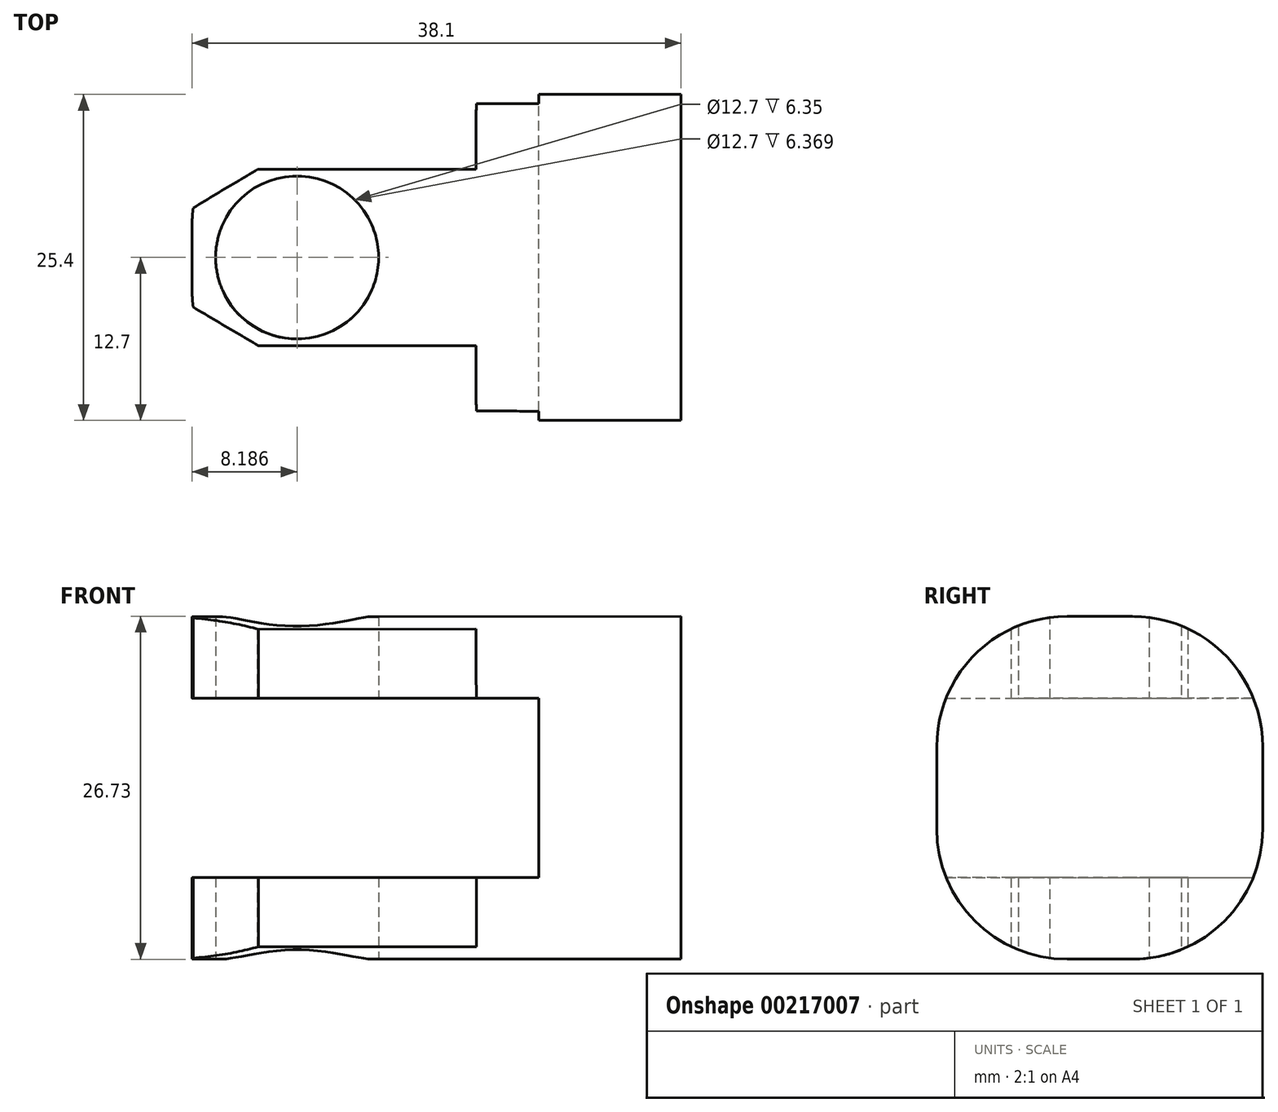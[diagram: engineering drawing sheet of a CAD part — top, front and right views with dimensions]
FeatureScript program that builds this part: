
annotation { "Feature Type Name" : "Feature", "Feature Type Description" : "" }
export const myFeature = defineFeature(function(context is Context, id is Id, definition is map)
    precondition{}
    {
        {
            var Q0;
            Q0=qCreatedBy(makeId("Front.planeOp"),FACE);
            var sketch = newSketch(context, id + "F0", { "sketchPlane" : qUnion([Q0])});
            skLineSegment(sketch, "E0.bottom", {"start": v(19.05, -6.98) * mm, "end": v(0, -6.99) * mm});
            skLineSegment(sketch, "E0.top", {"start": v(19.05, 6.99) * mm, "end": v(0, 6.99) * mm});
            skPoint(sketch, "E0.middle", {"position": v(0, 0) * mm});
            skLineSegment(sketch, "E1", {"start": v(0, 6.99) * mm, "end": v(0, 13.34) * mm});
            skLineSegment(sketch, "E2", {"start": v(0, -6.99) * mm, "end": v(0, -13.33) * mm});
            skLineSegment(sketch, "E3", {"start": v(0, -13.33) * mm, "end": v(38.1, -13.33) * mm});
            skLineSegment(sketch, "E4", {"start": v(38.1, -13.33) * mm, "end": v(38.1, 13.39) * mm});
            skLineSegment(sketch, "E5", {"start": v(38.1, 13.39) * mm, "end": v(0, 13.34) * mm});
            skPoint(sketch, "E0.right.end.orphan", {"position": v(-19.05, 6.99) * mm});
            skPoint(sketch, "E6.orphan", {"position": v(-19.05, -6.99) * mm});
            skLineSegment(sketch, "E7", {"start": v(19.05, 6.99) * mm, "end": v(27, 6.99) * mm});
            skLineSegment(sketch, "E8", {"start": v(27, 6.99) * mm, "end": v(27, -8.58) * mm});
            skLineSegment(sketch, "E9", {"start": v(19.05, -6.98) * mm, "end": v(27, -6.98) * mm});
            skSolve(sketch);
        }
        {
            var Q0;
            Q0 = qSketchRegion(id + "F0", true);
            extrude(context, id + "F1", {"entities" : qUnion([Q0]), "depth" : 25.4 * mm});
        }
        {
            var Q0;
            Q0=makeQuery(id+"F1.opExtrude","SWEPT_FACE",FACE,{"disambiguationData":[OSD([sQuery(id+"F0.wireOp",EDGE,"E3")])]});
            var sketch = newSketch(context, id + "F2", { "sketchPlane" : qUnion([Q0])});
            skCircle(sketch, "E10", {"center": v(8.19, 12.7) * mm, "radius": 6.35 * mm});
            skPoint(sketch, "E10.centerSnap0", {"position": v(0, 12.7) * mm});
            skSolve(sketch);
        }
        {
            var Q0;
            Q0=makeQuery(id+"F1.opExtrude","CAP_EDGE",EDGE,{"disambiguationData":[OSD([sQuery(id+"F0.wireOp",EDGE,"E2")])],"isStart":true});
            var Q1;
            Q1=makeQuery(id+"F1.opExtrude","CAP_EDGE",EDGE,{"disambiguationData":[OSD([sQuery(id+"F0.wireOp",EDGE,"E1")])],"isStart":true});
            var Q2;
            Q2=makeQuery(id+"F1.opExtrude","CAP_EDGE",EDGE,{"disambiguationData":[OSD([sQuery(id+"F0.wireOp",EDGE,"E1")])],"isStart":false});
            var Q3;
            Q3=makeQuery(id+"F1.opExtrude","CAP_EDGE",EDGE,{"disambiguationData":[OSD([sQuery(id+"F0.wireOp",EDGE,"E2")])],"isStart":false});
            fillet(context, id + "F3", {"entities" : qUnion([Q0, Q1, Q2, Q3]), "radius" : 10.16 * mm, "tangentPropagation" : true, "allowEdgeOverflow" : false});
        }
        {
            var Q0;
            Q0=makeQuery(id+"F2.imprint","IMPRINT",FACE,{"disambiguationData":[TD([[makeQuery(id+"F2.imprint","IMPRINT",EDGE,{"derivedFrom":sQuery(id+"F2.wireOp",EDGE,"E10")}),1.0]])]});
            extrude(context, id + "F4", {"entities" : qUnion([Q0]), "operationType" : NewBodyOperationType.REMOVE, "endBound" : BoundingType.THROUGH_ALL, "oppositeDirection" : true, "depth" : 25.4 * mm});
        }
        {
            var Q0;
            Q0=makeQuery(id+"F1.opExtrude","SWEPT_FACE",FACE,{"disambiguationData":[OSD([sQuery(id+"F0.wireOp",EDGE,"E5")])]});
            var sketch = newSketch(context, id + "F5", { "sketchPlane" : qUnion([Q0])});
            skLineSegment(sketch, "E11.bottom", {"start": v(22.15, -5.82) * mm, "end": v(-18.45, -5.82) * mm});
            skLineSegment(sketch, "E11.top", {"start": v(22.15, -19.58) * mm, "end": v(-18.45, -19.58) * mm});
            skLineSegment(sketch, "E11.left", {"start": v(22.15, -5.82) * mm, "end": v(22.15, -19.58) * mm});
            skLineSegment(sketch, "E11.right", {"start": v(-18.45, -5.82) * mm, "end": v(-18.45, -19.58) * mm});
            skPoint(sketch, "E11.middle", {"position": v(1.85, -12.7) * mm});
            skLineSegment(sketch, "E12", {"start": v(22.15, -19.58) * mm, "end": v(22.15, -25.4) * mm});
            skLineSegment(sketch, "E13", {"start": v(22.15, -5.82) * mm, "end": v(22.15, 0) * mm});
            skLineSegment(sketch, "E14", {"start": v(-6.3, -19.58) * mm, "end": v(17.98, -30.66) * mm});
            skLineSegment(sketch, "E15", {"start": v(17.98, -30.66) * mm, "end": v(22.15, -25.4) * mm});
            skLineSegment(sketch, "E16", {"start": v(-7.33, -5.82) * mm, "end": v(20.42, 6.01) * mm});
            skLineSegment(sketch, "E17", {"start": v(20.42, 6.01) * mm, "end": v(22.15, 0) * mm});
            skSolve(sketch);
        }
        {
            var Q0;
            {var subQ7=sQuery(id+"F5.wireOp",EDGE,"E16");Q0=makeQuery(id+"F5.imprint","IMPRINT",FACE,{"disambiguationData":[TD([[makeQuery(id+"F5.imprint","IMPRINT",EDGE,{"derivedFrom":subQ7}),-1.0]])]});}
            var Q1;
            {var subQ0=sQuery(id+"F5.wireOp",EDGE,"E13");Q1=makeQuery(id+"F5.imprint","IMPRINT",FACE,{"disambiguationData":[TD([[makeQuery(id+"F5.imprint","IMPRINT",EDGE,{"derivedFrom":subQ0}),1.0]])]});}
            var Q2;
            {var subQ0=sQuery(id+"F5.wireOp",EDGE,"E12");Q2=makeQuery(id+"F5.imprint","IMPRINT",FACE,{"disambiguationData":[TD([[makeQuery(id+"F5.imprint","IMPRINT",EDGE,{"derivedFrom":subQ0}),-1.0]])]});}
            var Q3;
            {var subQ6=sQuery(id+"F5.wireOp",EDGE,"E14");Q3=makeQuery(id+"F5.imprint","IMPRINT",FACE,{"disambiguationData":[TD([[makeQuery(id+"F5.imprint","IMPRINT",EDGE,{"derivedFrom":subQ6}),1.0]])]});}
            extrude(context, id + "F6", {"entities" : qUnion([Q0, Q1, Q2, Q3]), "operationType" : NewBodyOperationType.REMOVE, "endBound" : BoundingType.THROUGH_ALL, "oppositeDirection" : true, "depth" : 25.4 * mm});
        }
        {
            var Q0;
            Q0=makeQuery(id+"F1.opExtrude","CAP_EDGE",EDGE,{"disambiguationData":[OSD([sQuery(id+"F0.wireOp",EDGE,"E5")])],"isStart":false});
            var Q1;
            Q1=makeQuery(id+"F1.opExtrude","CAP_EDGE",EDGE,{"disambiguationData":[OSD([sQuery(id+"F0.wireOp",EDGE,"E5")])],"isStart":true});
            var Q2;
            Q2=makeQuery(id+"F1.opExtrude","CAP_EDGE",EDGE,{"disambiguationData":[OSD([sQuery(id+"F0.wireOp",EDGE,"E3")])],"isStart":true});
            var Q3;
            Q3=makeQuery(id+"F1.opExtrude","CAP_EDGE",EDGE,{"disambiguationData":[OSD([sQuery(id+"F0.wireOp",EDGE,"E3")])],"isStart":false});
            fillet(context, id + "F7", {"entities" : qUnion([Q0, Q1, Q2, Q3]), "radius" : 10.16 * mm, "tangentPropagation" : true, "allowEdgeOverflow" : false});
        }
        {
            var Q0;
            Q0=qCreatedBy(makeId("Top.planeOp"),FACE);
            var sketch = newSketch(context, id + "F8", { "sketchPlane" : qUnion([Q0])});
            skLineSegment(sketch, "E18", {"start": v(6.35, -5.07) * mm, "end": v(-2.7, -10.52) * mm});
            skLineSegment(sketch, "E19", {"start": v(-2.7, -10.52) * mm, "end": v(-2.7, -14.92) * mm});
            skLineSegment(sketch, "E20", {"start": v(-2.7, -14.92) * mm, "end": v(6.35, -20.28) * mm});
            skLineSegment(sketch, "E21", {"start": v(6.35, -20.28) * mm, "end": v(-5.74, -20.28) * mm});
            skLineSegment(sketch, "E22", {"start": v(-5.74, -20.28) * mm, "end": v(-5.74, -5.07) * mm});
            skLineSegment(sketch, "E23", {"start": v(-5.74, -5.07) * mm, "end": v(6.35, -5.07) * mm});
            skSolve(sketch);
        }
        {
            var Q0;
            Q0=makeQuery(id+"F8.imprint","IMPRINT",FACE,{"disambiguationData":[TD([[makeQuery(id+"F8.imprint","IMPRINT",EDGE,{"derivedFrom":sQuery(id+"F8.wireOp",EDGE,"E18")}),-1.0]])]});
            extrude(context, id + "F9", {"entities" : qUnion([Q0]), "operationType" : NewBodyOperationType.REMOVE, "oppositeDirection" : true, "depth" : 101.6 * mm, "symmetric" : true});
        }
    });
